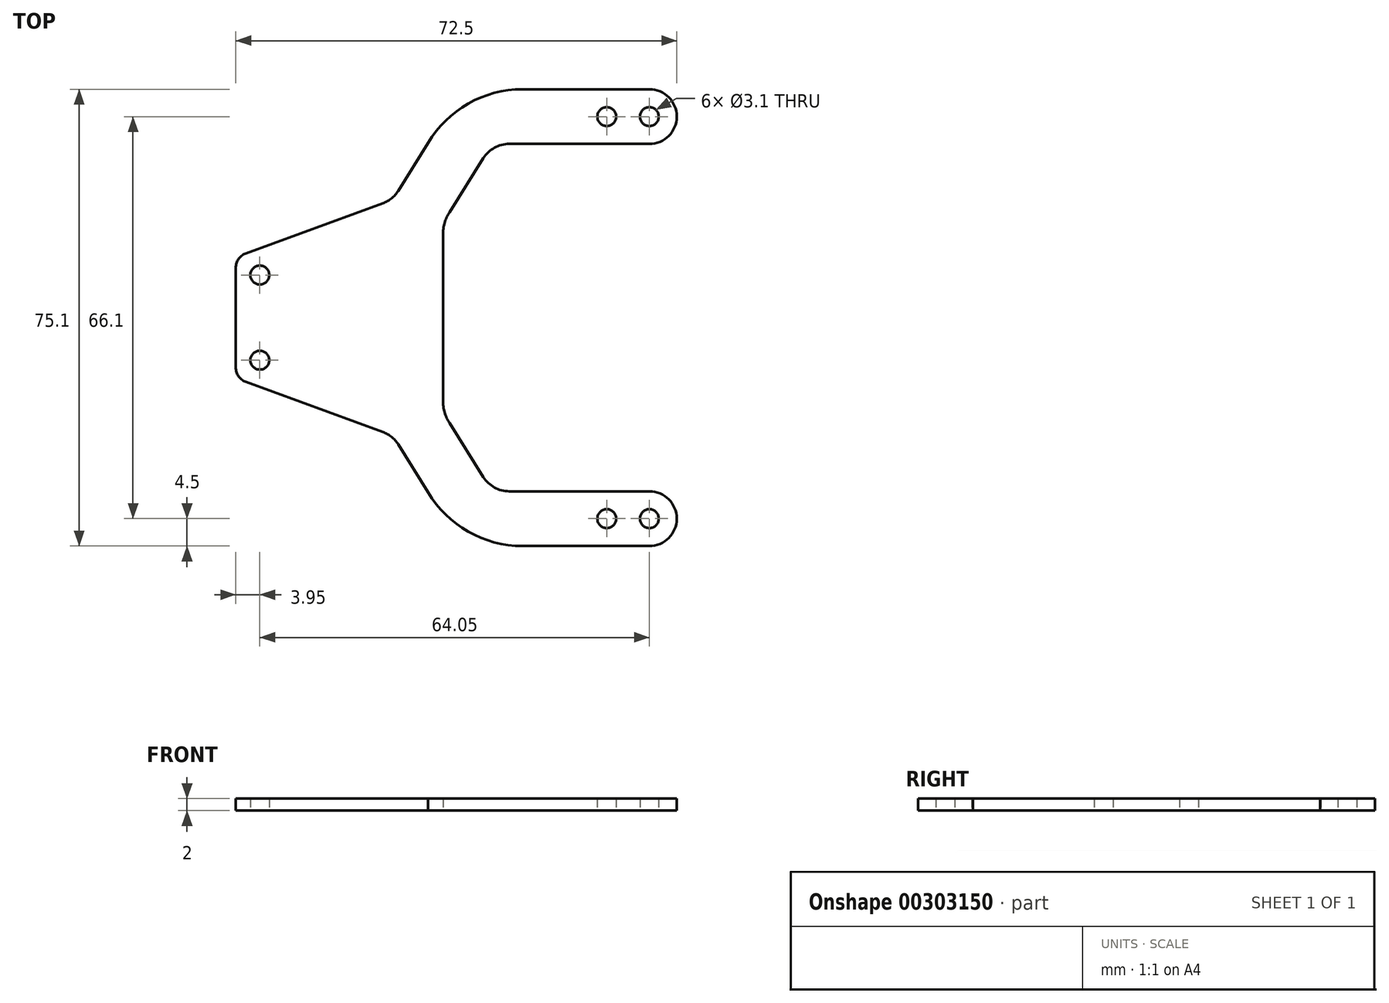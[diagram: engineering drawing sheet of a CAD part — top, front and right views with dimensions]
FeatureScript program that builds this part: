
annotation { "Feature Type Name" : "Feature", "Feature Type Description" : "" }
export const myFeature = defineFeature(function(context is Context, id is Id, definition is map)
    precondition{}
    {
        {
            var Q0;
            Q0=qCreatedBy(makeId("Top.planeOp"),FACE);
            var sketch = newSketch(context, id + "F0", { "sketchPlane" : qUnion([Q0])});
            skLineSegment(sketch, "E0.bottom", {"start": v(0, 0) * mm, "end": v(0, 0) * mm});
            skLineSegment(sketch, "E0.top", {"start": v(0, 0) * mm, "end": v(0, 0) * mm});
            skLineSegment(sketch, "E0.left", {"start": v(0, 0) * mm, "end": v(0, 0) * mm});
            skLineSegment(sketch, "E0.right", {"start": v(0, 0) * mm, "end": v(0, 0) * mm});
            skPoint(sketch, "E1.middle", {"position": v(0, 0) * mm});
            skLineSegment(sketch, "E2.top", {"start": v(48.5, 28.55) * mm, "end": v(25.44, 28.55) * mm});
            skLineSegment(sketch, "E2.left", {"start": v(53, 33.05) * mm, "end": v(53, 33.05) * mm});
            skArc(sketch, "E3.filletArc", {"start": v(53, 33.05) * mm, "mid": v(51.68, 36.23) * mm, "end": v(48.5, 37.55) * mm});
            skArc(sketch, "E4.filletArc", {"start": v(48.5, 28.55) * mm, "mid": v(51.68, 29.87) * mm, "end": v(53, 33.05) * mm});
            skCircle(sketch, "E5", {"center": v(48.5, 33.05) * mm, "radius": 1.55 * mm});
            skCircle(sketch, "E6", {"center": v(41.5, 33.05) * mm, "radius": 1.55 * mm});
            skCircle(sketch, "E7", {"center": v(-15.55, 7) * mm, "radius": 1.55 * mm});
            skLineSegment(sketch, "E8.MirrorCS", {"start": v(48.5, -28.55) * mm, "end": v(25.19, -28.55) * mm});
            skArc(sketch, "E9.MirrorCS", {"start": v(53, -33.05) * mm, "mid": v(51.68, -36.23) * mm, "end": v(48.5, -37.55) * mm});
            skArc(sketch, "E10.MirrorCS", {"start": v(48.5, -28.55) * mm, "mid": v(51.68, -29.87) * mm, "end": v(53, -33.05) * mm});
            skCircle(sketch, "E11.MirrorC", {"center": v(48.5, -33.05) * mm, "radius": 1.55 * mm});
            skCircle(sketch, "E12.MirrorC", {"center": v(41.5, -33.05) * mm, "radius": 1.55 * mm});
            skPoint(sketch, "E13.visualSharp", {"position": v(6.3, 19.4) * mm});
            skCircle(sketch, "E14", {"center": v(-15.55, -7) * mm, "radius": 1.55 * mm});
            skPoint(sketch, "E15.newPointA", {"position": v(-19.5, 9.16) * mm});
            skArc(sketch, "E15.filletArc", {"start": v(-17.86, 10.55) * mm, "mid": v(-19.05, 9.63) * mm, "end": v(-19.5, 8.2) * mm});
            skArc(sketch, "E16.MirrorCS", {"start": v(-17.86, -10.55) * mm, "mid": v(-19.05, -9.63) * mm, "end": v(-19.5, -8.2) * mm});
            skLineSegment(sketch, "E17", {"start": v(-19.5, 8.2) * mm, "end": v(-19.5, -8.2) * mm});
            skLineSegment(sketch, "E18", {"start": v(27.64, 37.55) * mm, "end": v(48.5, 37.55) * mm});
            skPoint(sketch, "E19.visualSharp", {"position": v(17.36, 37.55) * mm});
            skArc(sketch, "E19.filletArc", {"start": v(27.64, 37.55) * mm, "mid": v(18.71, 35.18) * mm, "end": v(12.13, 28.69) * mm});
            skLineSegment(sketch, "E20", {"start": v(-17.86, 10.55) * mm, "end": v(4.69, 18.8) * mm});
            skLineSegment(sketch, "E21", {"start": v(12.13, 28.69) * mm, "end": v(7.2, 20.84) * mm});
            skArc(sketch, "E22.filletArc", {"start": v(4.69, 18.8) * mm, "mid": v(6.11, 19.62) * mm, "end": v(7.2, 20.84) * mm});
            skLineSegment(sketch, "E23.MirrorCS", {"start": v(-17.86, -10.55) * mm, "end": v(4.69, -18.8) * mm});
            skLineSegment(sketch, "E24.MirrorCS", {"start": v(12.13, -28.69) * mm, "end": v(7.2, -20.84) * mm});
            skArc(sketch, "E25.MirrorCS", {"start": v(27.64, -37.55) * mm, "mid": v(18.71, -35.18) * mm, "end": v(12.13, -28.69) * mm});
            skLineSegment(sketch, "E26.MirrorCS", {"start": v(27.64, -37.55) * mm, "end": v(48.5, -37.55) * mm});
            skArc(sketch, "E27.MirrorCS", {"start": v(4.69, -18.8) * mm, "mid": v(6.11, -19.62) * mm, "end": v(7.2, -20.84) * mm});
            skLineSegment(sketch, "E28", {"start": v(21.21, 26.21) * mm, "end": v(15.64, 17.36) * mm});
            skPoint(sketch, "E29.newPointB", {"position": v(25.19, 28.55) * mm});
            skArc(sketch, "E29.filletArc", {"start": v(25.44, 28.55) * mm, "mid": v(23.03, 27.93) * mm, "end": v(21.21, 26.21) * mm});
            skLineSegment(sketch, "E30.MirrorCS", {"start": v(21.21, -26.21) * mm, "end": v(15.64, -17.36) * mm});
            skArc(sketch, "E31.MirrorCS", {"start": v(25.44, -28.55) * mm, "mid": v(23.03, -27.93) * mm, "end": v(21.21, -26.21) * mm});
            skLineSegment(sketch, "E32", {"start": v(14.57, 13.63) * mm, "end": v(14.57, -13.63) * mm});
            skPoint(sketch, "E33.visualSharp", {"position": v(14.57, 15.65) * mm});
            skArc(sketch, "E33.filletArc", {"start": v(15.64, 17.36) * mm, "mid": v(14.84, 15.57) * mm, "end": v(14.57, 13.63) * mm});
            skPoint(sketch, "E34.visualSharp", {"position": v(14.57, -15.65) * mm});
            skArc(sketch, "E34.filletArc", {"start": v(14.57, -13.63) * mm, "mid": v(14.84, -15.57) * mm, "end": v(15.64, -17.36) * mm});
            skSolve(sketch);
        }
        {
            var Q0;
            Q0=makeQuery(id+"F0.imprint","IMPRINT",FACE,{"disambiguationData":[TD([[makeQuery(id+"F0.imprint","IMPRINT",EDGE,{"derivedFrom":sQuery(id+"F0.wireOp",EDGE,"E2.bottom")}),1.0]])]});
            var Q1;
            Q1=makeQuery(id+"F0.imprint","IMPRINT",FACE,{"disambiguationData":[TD([[makeQuery(id+"F0.imprint","IMPRINT",EDGE,{"derivedFrom":sQuery(id+"F0.wireOp",EDGE,"E2.top")}),-1.0]])]});
            extrude(context, id + "F1", {"entities" : qUnion([Q0, Q1]), "depth" : 2 * mm});
        }
    });
